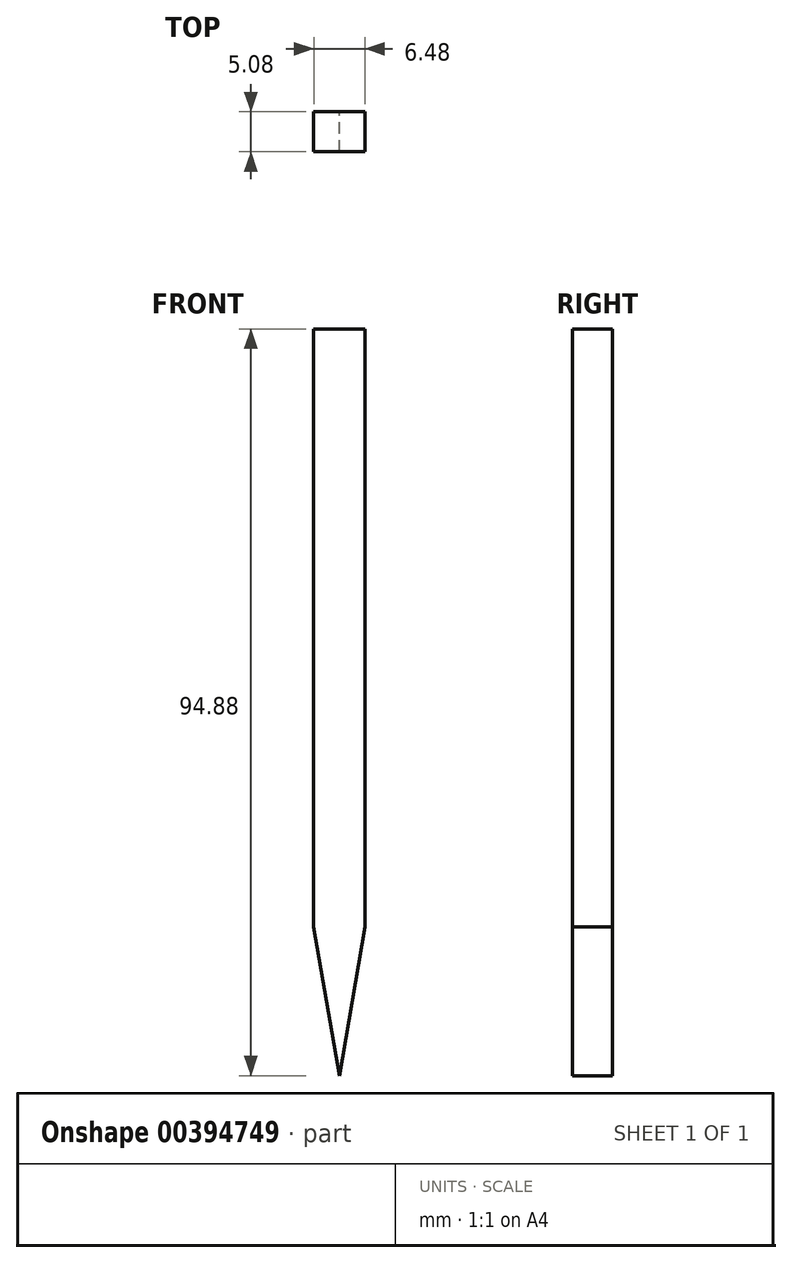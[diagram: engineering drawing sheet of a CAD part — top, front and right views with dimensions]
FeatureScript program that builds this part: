
annotation { "Feature Type Name" : "Feature", "Feature Type Description" : "" }
export const myFeature = defineFeature(function(context is Context, id is Id, definition is map)
    precondition{}
    {
        {
            var Q0;
            Q0=qCreatedBy(makeId("Front.planeOp"),FACE);
            var sketch = newSketch(context, id + "F0", { "sketchPlane" : qUnion([Q0])});
            skLineSegment(sketch, "E0.bottom", {"start": v(-3.24, 37.98) * mm, "end": v(3.24, 37.98) * mm});
            skLineSegment(sketch, "E0.top", {"start": v(-3.24, -37.98) * mm, "end": v(3.24, -37.98) * mm});
            skLineSegment(sketch, "E0.left", {"start": v(-3.24, 37.98) * mm, "end": v(-3.24, -37.98) * mm});
            skLineSegment(sketch, "E0.right", {"start": v(3.24, 37.98) * mm, "end": v(3.24, -37.98) * mm});
            skPoint(sketch, "E0.middle", {"position": v(0, 0) * mm});
            skLineSegment(sketch, "E1", {"start": v(-3.24, -37.98) * mm, "end": v(0, -56.9) * mm});
            skPoint(sketch, "E1.endSnap0", {"position": v(0, -37.98) * mm});
            skLineSegment(sketch, "E2", {"start": v(0, -56.9) * mm, "end": v(3.24, -37.98) * mm});
            skSolve(sketch);
        }
        {
            var Q0;
            Q0=makeQuery(id+"F0.imprint","IMPRINT",FACE,{"disambiguationData":[TD([[makeQuery(id+"F0.imprint","IMPRINT",EDGE,{"derivedFrom":sQuery(id+"F0.wireOp",EDGE,"E0.bottom")}),-1.0]])]});
            var Q1;
            Q1=makeQuery(id+"F0.imprint","IMPRINT",FACE,{"disambiguationData":[TD([[makeQuery(id+"F0.imprint","IMPRINT",EDGE,{"derivedFrom":sQuery(id+"F0.wireOp",EDGE,"E0.top")}),-1.0]])]});
            extrude(context, id + "F1", {"entities" : qUnion([Q0, Q1]), "depth" : 5.08 * mm});
        }
    });
